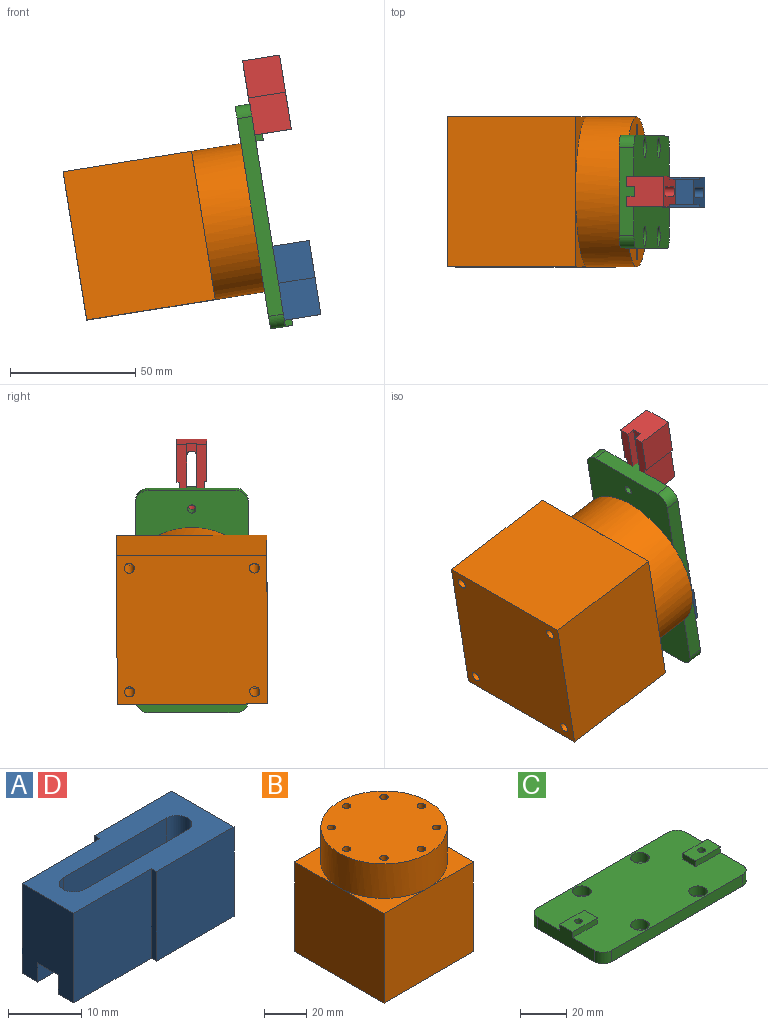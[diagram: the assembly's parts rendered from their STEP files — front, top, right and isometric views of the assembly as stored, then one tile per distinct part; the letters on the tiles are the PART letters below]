
ASSEMBLY  parts=4 mates=3
PART A: 17 faces, bbox 30x12x15 mm
  f0: plane 30x4mm, normal (0,0,-1), area 105mm2, adj f1,f4,f8,f9,f10,f12
  f1: plane 15x12mm, normal (1,0,0), area 167.2mm2, adj f0,f7,f8,f10,f11,f13,f14,f15
  f2: cylinder r=2mm len=11.8mm, axis (0,0,-1), area 74.1mm2, adj f10,f11,f13,f16
  f3: cylinder r=2mm len=11.8mm, axis (0,0,-1), area 74.1mm2, adj f10,f11,f13,f15
  f4: plane 15x10mm, normal (-1,0,0), area 137.2mm2, adj f0,f5,f10,f11,f12,f13,f14,f16
  f5: plane 15x15mm, normal (0,-1,0), area 225mm2, adj f4,f6,f13,f14
  f6: plane 15x1mm, normal (-1,0,0), area 15mm2, adj f5,f7,f13,f14
  f7: plane 15x15mm, normal (0,-1,0), area 225mm2, adj f1,f6,f13,f14
  f8: plane 15x15mm, normal (0,1,0), area 225mm2, adj f0,f1,f9,f13
  f9: plane 15x1mm, normal (-1,0,0), area 15mm2, adj f0,f8,f12,f13
  f10: plane 30x15mm, normal (0,-1,0), area 332mm2, adj f0,f1,f2,f3,f4,f13,f15,f16
  f11: plane 30x15mm, normal (0,1,0), area 332mm2, adj f1,f2,f3,f4,f13,f14,f15,f16
  f12: plane 15x15mm, normal (0,1,0), area 225mm2, adj f0,f4,f9,f13
  f13: plane 30x12mm, normal (0,0,1), area 237.4mm2, adj f1,f2,f3,f4,f5,f6,f7,f8
  f14: plane 30x4mm, normal (0,0,-1), area 105mm2, adj f1,f4,f5,f6,f7,f11
  f15: plane 5x4mm, normal (0,0,-1), area 13.7mm2, adj f1,f3,f10,f11
  f16: plane 5x4mm, normal (0,0,-1), area 13.7mm2, adj f2,f4,f10,f11
PART B: 35 faces, bbox 60x60x72 mm
  f0: plane 60x60mm, normal (0,0,-1), area 3549.7mm2, adj f4,f5,f6,f7,f27,f29,f31,f33
  f1: plane 30x30mm, normal (0,0,1), area 193.1mm2, adj f4,f7,f9
  f2: plane 30x30mm, normal (0,0,1), area 193.1mm2, adj f4,f5,f9
  f3: plane 30x30mm, normal (0,0,1), area 193.1mm2, adj f5,f6,f9
  f4: plane 60x52mm, normal (0,1,0), area 3120mm2, adj f0,f1,f2,f5,f7
  f5: plane 60x52mm, normal (-1,0,0), area 3120mm2, adj f0,f2,f3,f4,f6
  f6: plane 60x52mm, normal (0,-1,0), area 3120mm2, adj f0,f3,f5,f7,f8
  f7: plane 60x52mm, normal (1,0,0), area 3120mm2, adj f0,f1,f4,f6,f8
  f8: plane 30x30mm, normal (0,0,1), area 193.1mm2, adj f6,f7,f9
  f9: cylinder r=30mm len=60mm, axis (0,0,-1), area 3769.9mm2, adj f1,f2,f3,f8,f10
  f10: plane 60x60mm, normal (0,0,1), area 2726.9mm2, adj f9,f11,f13,f15,f17,f19,f21,f23
  f11: cylinder r=2mm len=5mm, axis (0,0,1), area 62.8mm2, adj f10,f12
  f12: plane 4x4mm, normal (0,0,1), area 12.6mm2, adj f11
  f13: cylinder r=2mm len=5mm, axis (0,0,1), area 62.8mm2, adj f10,f14
  f14: plane 4x4mm, normal (0,0,1), area 12.6mm2, adj f13
  f15: cylinder r=2mm len=5mm, axis (0,0,1), area 62.8mm2, adj f10,f16
  f16: plane 4x4mm, normal (0,0,1), area 12.6mm2, adj f15
  f17: cylinder r=2mm len=5mm, axis (0,0,1), area 62.8mm2, adj f10,f18
  f18: plane 4x4mm, normal (0,0,1), area 12.6mm2, adj f17
  f19: cylinder r=2mm len=5mm, axis (0,0,1), area 62.8mm2, adj f10,f20
  f20: plane 4x4mm, normal (0,0,1), area 12.6mm2, adj f19
  f21: cylinder r=2mm len=5mm, axis (0,0,1), area 62.8mm2, adj f10,f22
  f22: plane 4x4mm, normal (0,0,1), area 12.6mm2, adj f21
  f23: cylinder r=2mm len=5mm, axis (0,0,1), area 62.8mm2, adj f10,f24
  f24: plane 4x4mm, normal (0,0,1), area 12.6mm2, adj f23
  f25: cylinder r=2mm len=5mm, axis (0,0,1), area 62.8mm2, adj f10,f26
  f26: plane 4x4mm, normal (0,0,1), area 12.6mm2, adj f25
  f27: cylinder r=2mm len=20mm, axis (0,0,-1), area 251.3mm2, adj f0,f28
  f28: plane 4x4mm, normal (0,0,-1), area 12.6mm2, adj f27
  f29: cylinder r=2mm len=20mm, axis (0,0,-1), area 251.3mm2, adj f0,f30
  f30: plane 4x4mm, normal (0,0,-1), area 12.6mm2, adj f29
  f31: cylinder r=2mm len=20mm, axis (0,0,-1), area 251.3mm2, adj f0,f32
  f32: plane 4x4mm, normal (0,0,-1), area 12.6mm2, adj f31
  f33: cylinder r=2mm len=20mm, axis (0,0,-1), area 251.3mm2, adj f0,f34
  f34: plane 4x4mm, normal (0,0,-1), area 12.6mm2, adj f33
PART C: 32 faces, bbox 90x45x9 mm
  f0: plane 90x45mm, normal (0,0,1), area 3587.5mm2, adj f5,f6,f7,f8,f9,f10,f11,f14
  f1: cylinder r=2mm len=4mm, axis (0,0,1), area 12.6mm2, adj f15,f19
  f2: cylinder r=2mm len=4mm, axis (0,0,1), area 12.6mm2, adj f15,f21
  f3: cylinder r=2mm len=4mm, axis (0,0,1), area 12.6mm2, adj f15,f23
  f4: cylinder r=1.65mm len=3.3mm, axis (0,0,1), area 10.4mm2, adj f15,f16
  f5: cylinder r=5mm len=6mm, axis (0,0,1), area 47.1mm2, adj f0,f6,f14,f15
  f6: plane 35x9mm, normal (-1,0,0), area 234mm2, adj f0,f5,f7,f15,f24,f25,f27
  f7: cylinder r=5mm len=6mm, axis (0,0,1), area 47.1mm2, adj f0,f6,f8,f15
  f8: plane 80x6mm, normal (0,-1,0), area 480mm2, adj f0,f7,f9,f15
  f9: cylinder r=5mm len=6mm, axis (0,0,1), area 47.1mm2, adj f0,f8,f10,f15
  f10: plane 35x9mm, normal (1,0,0), area 234mm2, adj f0,f9,f11,f15,f28,f30,f31
  f11: cylinder r=5mm len=6mm, axis (0,0,1), area 47.1mm2, adj f0,f10,f14,f15
  f12: cylinder r=1.65mm len=9mm, axis (0,0,1), area 93.3mm2, adj f15,f31
  f13: cylinder r=1.65mm len=9mm, axis (0,0,1), area 93.3mm2, adj f15,f27
  f14: plane 80x6mm, normal (0,1,0), area 480mm2, adj f0,f5,f11,f15
  f15: plane 90x45mm, normal (0,0,-1), area 3965.2mm2, adj f1,f2,f3,f4,f5,f6,f7,f8
  f16: plane 8x8mm, normal (0,0,1), area 41.7mm2, adj f4,f17
  f17: cylinder r=4mm len=8mm, axis (0,0,1), area 125.7mm2, adj f0,f16
  f18: cylinder r=4mm len=8mm, axis (0,0,1), area 125.7mm2, adj f0,f19
  f19: plane 8x8mm, normal (0,0,1), area 37.7mm2, adj f1,f18
  f20: cylinder r=4mm len=8mm, axis (0,0,1), area 125.7mm2, adj f0,f21
  f21: plane 8x8mm, normal (0,0,1), area 37.7mm2, adj f2,f20
  f22: cylinder r=4mm len=8mm, axis (0,0,1), area 125.7mm2, adj f0,f23
  f23: plane 8x8mm, normal (0,0,1), area 37.7mm2, adj f3,f22
  f24: plane 15x3mm, normal (0,1,0), area 45mm2, adj f0,f6,f26,f27
  f25: plane 15x3mm, normal (0,-1,0), area 45mm2, adj f0,f6,f26,f27
  f26: plane 8x3mm, normal (1,0,0), area 24mm2, adj f0,f24,f25,f27
  f27: plane 15x8mm, normal (0,0,1), area 111.4mm2, adj f6,f13,f24,f25,f26
  f28: plane 15x3mm, normal (0,1,0), area 45mm2, adj f0,f10,f29,f31
  f29: plane 8x3mm, normal (-1,0,0), area 24mm2, adj f0,f28,f30,f31
  f30: plane 15x3mm, normal (0,-1,0), area 45mm2, adj f0,f10,f29,f31
  f31: plane 15x8mm, normal (0,0,1), area 111.4mm2, adj f10,f12,f28,f29,f30
PART D: same geometry as A
PLACE A rot(axis=(0,1,0),81deg) t=(23.48,72.45,-19.16)mm
PLACE B rot(axis=(0,1,0),81deg) t=(-6.32,72.52,3.96)mm fixed
PLACE C rot(axis=(0,1,0),81deg) t=(19.36,72.5,8.03)mm
PLACE D rot(axis=(0.65,0,0.76),179.9deg) t=(11.69,72.6,54.91)mm
MATE pin_slot C.f15 <-> B.f9  axis (-0.99,0,-0.16) through (13.43,72.52,7.1)mm
MATE pin_slot A.f2 <-> C.f12  axis (-0.99,0,-0.16) through (25.07,72.47,-8.78)mm
MATE pin_slot D.f2 <-> C.f13  axis (-0.99,0,-0.16) through (16.42,72.58,45.53)mm
